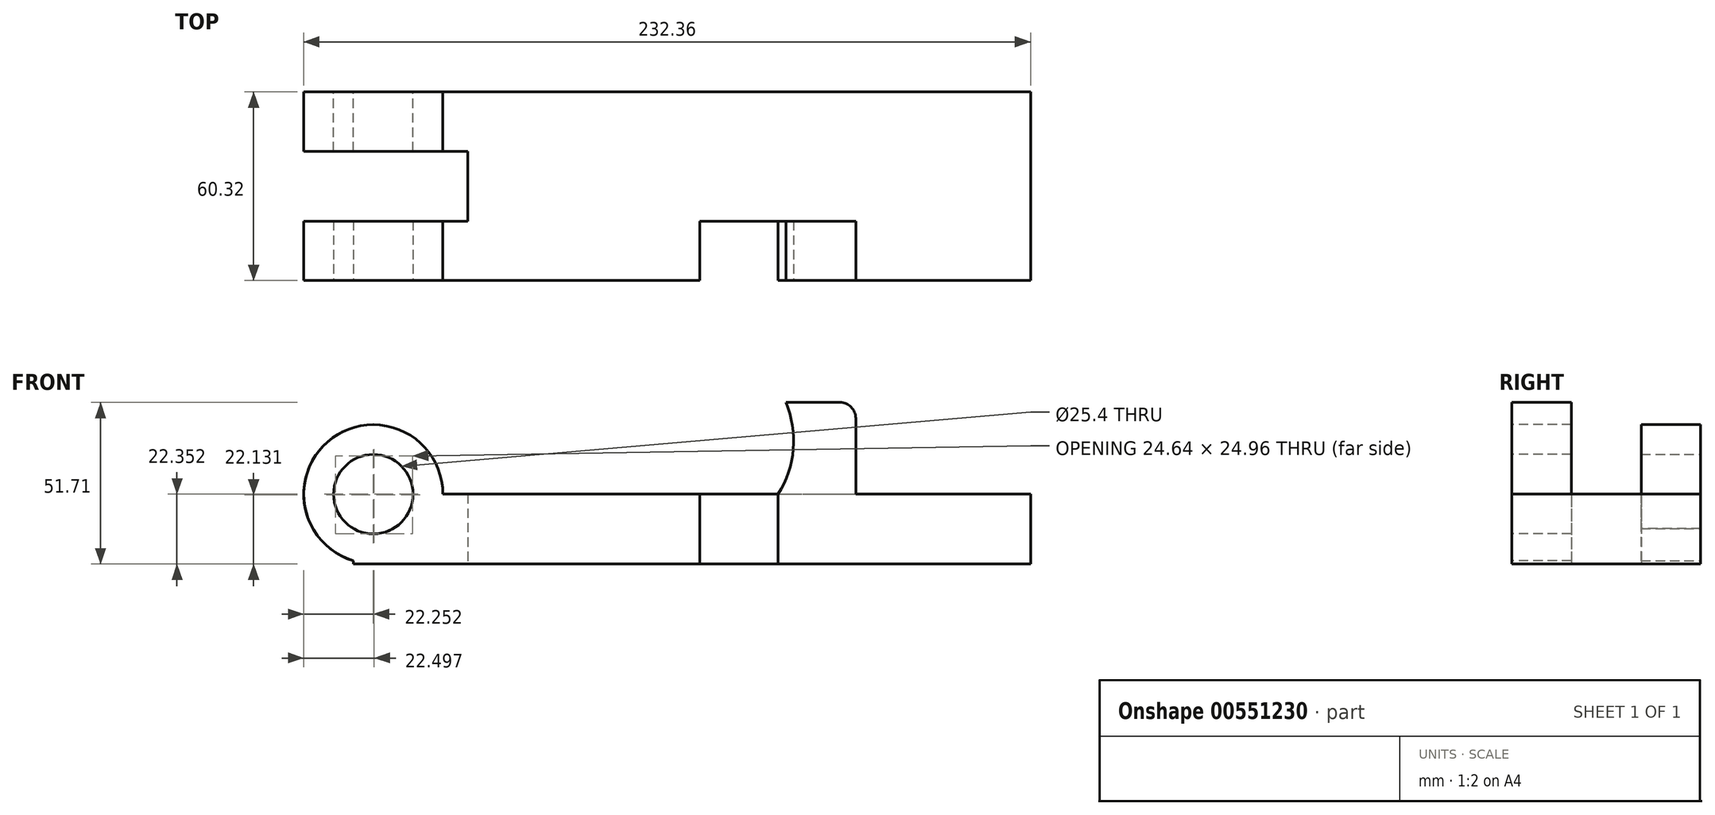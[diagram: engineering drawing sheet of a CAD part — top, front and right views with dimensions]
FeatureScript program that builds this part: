
annotation { "Feature Type Name" : "Feature", "Feature Type Description" : "" }
export const myFeature = defineFeature(function(context is Context, id is Id, definition is map)
    precondition{}
    {
        {
            var Q0;
            Q0=qCreatedBy(makeId("Top.planeOp"),FACE);
            var sketch = newSketch(context, id + "F0", { "sketchPlane" : qUnion([Q0])});
            skLineSegment(sketch, "E0", {"start": v(-110.74, 17.58) * mm, "end": v(105.82, 17.58) * mm});
            skLineSegment(sketch, "E1", {"start": v(105.82, 17.58) * mm, "end": v(105.82, -42.74) * mm});
            skLineSegment(sketch, "E2", {"start": v(-110.74, -42.74) * mm, "end": v(-110.74, -23.74) * mm});
            skLineSegment(sketch, "E3", {"start": v(-110.74, -23.74) * mm, "end": v(-74.07, -23.74) * mm});
            skLineSegment(sketch, "E4", {"start": v(-74.07, -23.74) * mm, "end": v(-74.07, -1.42) * mm});
            skLineSegment(sketch, "E5", {"start": v(-74.07, -1.42) * mm, "end": v(-110.74, -1.42) * mm});
            skLineSegment(sketch, "E6", {"start": v(-110.74, -1.42) * mm, "end": v(-110.74, 17.58) * mm});
            skLineSegment(sketch, "E7", {"start": v(-110.74, -42.74) * mm, "end": v(0, -42.74) * mm});
            skLineSegment(sketch, "E8", {"start": v(0, -42.74) * mm, "end": v(0, -23.74) * mm});
            skLineSegment(sketch, "E9", {"start": v(0, -23.74) * mm, "end": v(25.14, -23.74) * mm});
            skLineSegment(sketch, "E10", {"start": v(25.14, -23.74) * mm, "end": v(25.14, -42.74) * mm});
            skLineSegment(sketch, "E11", {"start": v(25.14, -42.74) * mm, "end": v(105.82, -42.74) * mm});
            skSolve(sketch);
        }
        {
            var Q0;
            Q0=qSketchRegion(id+"F0",true);
            extrude(context, id + "F1", {"entities" : qUnion([Q0]), "depth" : 22.35 * mm, "offsetDistance" : 25.4 * mm});
        }
        {
            var Q0;
            Q0=makeQuery(id+"F1.opExtrude","SWEPT_FACE",FACE,{"disambiguationData":[OSD([sQuery(id+"F0.wireOp",EDGE,"E7")])]});
            var sketch = newSketch(context, id + "F2", { "sketchPlane" : qUnion([Q0])});
            skCircle(sketch, "E12", {"center": v(-104.29, 22.35) * mm, "radius": 22.23 * mm});
            skCircle(sketch, "E13", {"center": v(-104.29, 22.35) * mm, "radius": 12.7 * mm});
            skSolve(sketch);
        }
        {
            var Q0;
            Q0=makeQuery(id+"F1.opExtrude","SWEPT_FACE",FACE,{"disambiguationData":[OSD([sQuery(id+"F0.wireOp",EDGE,"E0")])]});
            var sketch = newSketch(context, id + "F3", { "sketchPlane" : qUnion([Q0])});
            skCircle(sketch, "E14", {"center": v(104.31, 22.35) * mm, "radius": 22.23 * mm});
            skCircle(sketch, "E15", {"center": v(104.31, 22.35) * mm, "radius": 12.7 * mm});
            skSolve(sketch);
        }
        {
            var Q0;
            {var subQ0=sQuery(id+"F2.wireOp",EDGE,"E13");var subQ1=sQuery(id+"F0.wireOp",EDGE,"E7");var subQ4=makeQuery(id+"F1.opExtrude","CAP_EDGE",EDGE,{"disambiguationData":[OSD([subQ1])],"isStart":false});var subQ5=makeQuery(id+"F2.imprint","INTERSECT",VERTEX,{"derivedFrom":[subQ4,subQ0]});Q0=makeQuery(id+"F2.imprint","IMPRINT",FACE,{"disambiguationData":[TD([[makeQuery(id+"F2.imprint","IMPRINT",EDGE,{"disambiguationData":[TD([[subQ5,1.0]])],"derivedFrom":subQ0}),1.0]])]});}
            extrude(context, id + "F4", {"entities" : qUnion([Q0]), "operationType" : NewBodyOperationType.REMOVE, "endBound" : BoundingType.THROUGH_ALL, "oppositeDirection" : true, "depth" : 25.4 * mm, "offsetDistance" : 25.4 * mm});
        }
        {
            var Q0;
            {var subQ0=sQuery(id+"F2.wireOp",EDGE,"E12");var subQ1=sQuery(id+"F0.wireOp",EDGE,"E7");var subQ4=makeQuery(id+"F1.opExtrude","CAP_EDGE",EDGE,{"disambiguationData":[OSD([subQ1])],"isStart":false});var subQ5=makeQuery(id+"F2.imprint","INTERSECT",VERTEX,{"derivedFrom":[subQ4,subQ0]});Q0=makeQuery(id+"F2.imprint","IMPRINT",FACE,{"disambiguationData":[TD([[makeQuery(id+"F2.imprint","IMPRINT",EDGE,{"disambiguationData":[TD([[subQ5,1.0]])],"derivedFrom":subQ4}),-1.0]])]});}
            var Q1;
            {var subQ0=sQuery(id+"F2.wireOp",EDGE,"E12");var subQ1=sQuery(id+"F0.wireOp",EDGE,"E7");var subQ4=makeQuery(id+"F1.opExtrude","CAP_EDGE",EDGE,{"disambiguationData":[OSD([subQ1])],"isStart":false});var subQ5=makeQuery(id+"F2.imprint","INTERSECT",VERTEX,{"derivedFrom":[subQ4,subQ0]});Q1=makeQuery(id+"F2.imprint","IMPRINT",FACE,{"disambiguationData":[TD([[makeQuery(id+"F2.imprint","IMPRINT",EDGE,{"disambiguationData":[TD([[subQ5,1.0]])],"derivedFrom":subQ4}),1.0]])]});}
            extrude(context, id + "F5", {"entities" : qUnion([Q0, Q1]), "operationType" : NewBodyOperationType.ADD, "oppositeDirection" : true, "depth" : 19 * mm, "offsetDistance" : 25.4 * mm});
        }
        {
            var Q0;
            {var subQ0=sQuery(id+"F3.wireOp",EDGE,"E14");var subQ1=sQuery(id+"F0.wireOp",EDGE,"E0");var subQ4=makeQuery(id+"F1.opExtrude","CAP_EDGE",EDGE,{"disambiguationData":[OSD([subQ1])],"isStart":false});var subQ5=makeQuery(id+"F3.imprint","INTERSECT",VERTEX,{"derivedFrom":[subQ4,subQ0]});Q0=makeQuery(id+"F3.imprint","IMPRINT",FACE,{"disambiguationData":[TD([[makeQuery(id+"F3.imprint","IMPRINT",EDGE,{"disambiguationData":[TD([[subQ5,1.0]])],"derivedFrom":subQ4}),1.0]])]});}
            var Q1;
            {var subQ0=sQuery(id+"F3.wireOp",EDGE,"E14");var subQ1=sQuery(id+"F0.wireOp",EDGE,"E0");var subQ4=makeQuery(id+"F1.opExtrude","CAP_EDGE",EDGE,{"disambiguationData":[OSD([subQ1])],"isStart":false});var subQ5=makeQuery(id+"F3.imprint","INTERSECT",VERTEX,{"derivedFrom":[subQ4,subQ0]});Q1=makeQuery(id+"F3.imprint","IMPRINT",FACE,{"disambiguationData":[TD([[makeQuery(id+"F3.imprint","IMPRINT",EDGE,{"disambiguationData":[TD([[subQ5,1.0]])],"derivedFrom":subQ4}),-1.0]])]});}
            extrude(context, id + "F6", {"entities" : qUnion([Q0, Q1]), "operationType" : NewBodyOperationType.ADD, "oppositeDirection" : true, "depth" : 19 * mm, "offsetDistance" : 25.4 * mm});
        }
        {
            var Q0;
            Q0=makeQuery(id+"F1.opExtrude","SWEPT_FACE",FACE,{"disambiguationData":[OSD([sQuery(id+"F0.wireOp",EDGE,"E11")])]});
            var sketch = newSketch(context, id + "F7", { "sketchPlane" : qUnion([Q0])});
            skLineSegment(sketch, "E16", {"start": v(27.57, 51.7) * mm, "end": v(44.85, 51.7) * mm});
            skLineSegment(sketch, "E17", {"start": v(49.93, 46.63) * mm, "end": v(49.93, 22.35) * mm});
            skLineSegment(sketch, "E18", {"start": v(49.93, 22.35) * mm, "end": v(25.14, 22.35) * mm});
            skArc(sketch, "E19", {"start": v(25.14, 22.35) * mm, "mid": v(29.97, 36.73) * mm, "end": v(27.57, 51.7) * mm});
            skPoint(sketch, "E20.visualSharp", {"position": v(49.93, 51.7) * mm});
            skArc(sketch, "E20.filletArc", {"start": v(49.93, 46.63) * mm, "mid": v(48.44, 50.22) * mm, "end": v(44.85, 51.7) * mm});
            skSolve(sketch);
        }
        {
            var Q0;
            Q0=qSketchRegion(id+"F7",true);
            extrude(context, id + "F8", {"entities" : qUnion([Q0]), "operationType" : NewBodyOperationType.ADD, "oppositeDirection" : true, "depth" : 19 * mm, "offsetDistance" : 25.4 * mm});
        }
    });
